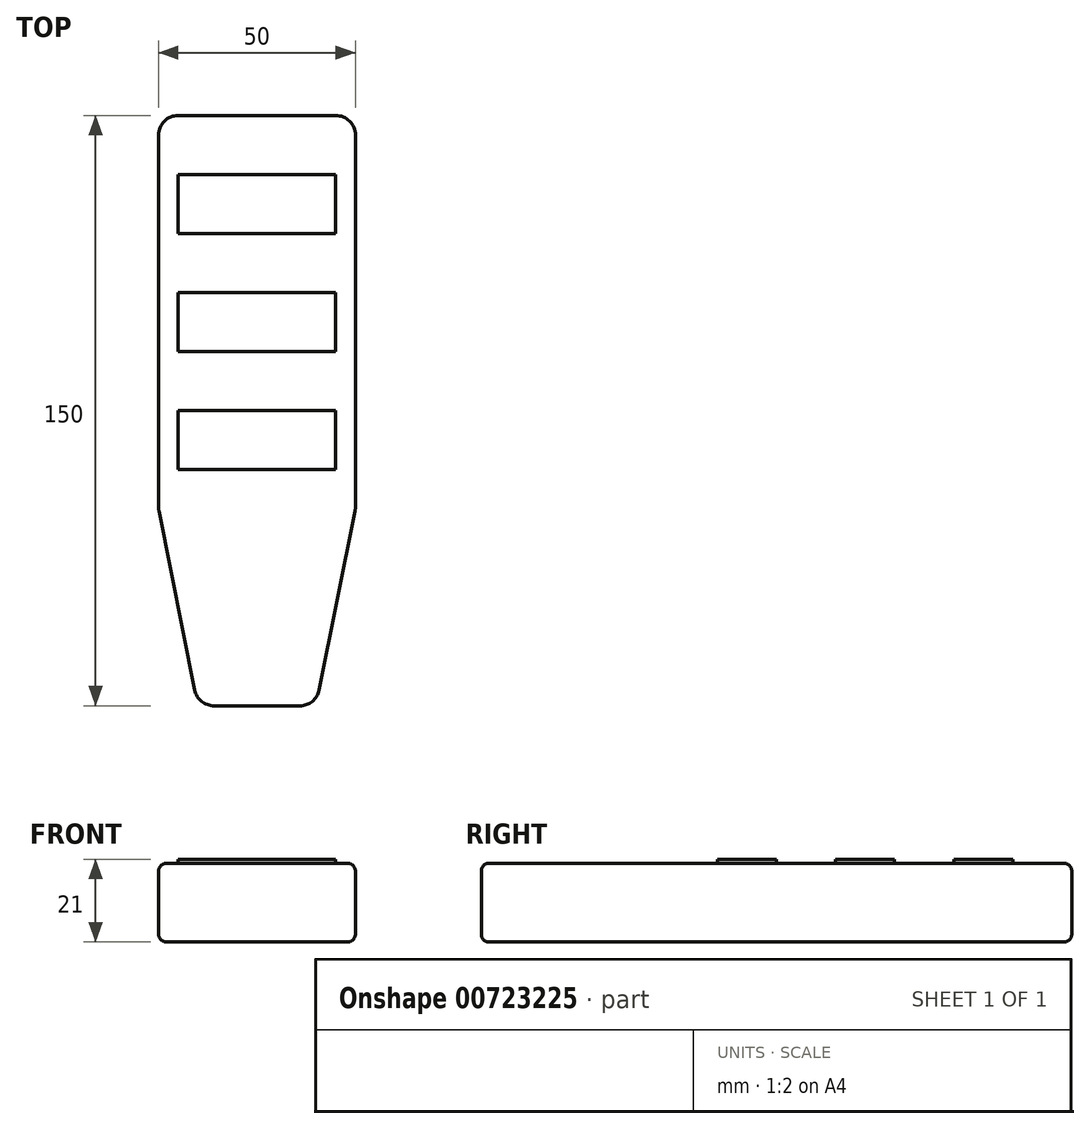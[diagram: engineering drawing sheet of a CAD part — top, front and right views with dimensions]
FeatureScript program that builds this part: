
annotation { "Feature Type Name" : "Feature", "Feature Type Description" : "" }
export const myFeature = defineFeature(function(context is Context, id is Id, definition is map)
    precondition{}
    {
        {
            var Q0;
            Q0=qCreatedBy(makeId("Top.planeOp"),FACE);
            var sketch = newSketch(context, id + "F0", { "sketchPlane" : qUnion([Q0])});
            skLineSegment(sketch, "E0.bottom", {"start": v(-20, 75) * mm, "end": v(20, 75) * mm});
            skLineSegment(sketch, "E0.top", {"start": v(-10.9, -75) * mm, "end": v(10.9, -75) * mm});
            skLineSegment(sketch, "E0.left", {"start": v(-25, 70) * mm, "end": v(-25, -24.5) * mm});
            skLineSegment(sketch, "E0.right", {"start": v(25, 70) * mm, "end": v(25, -24.5) * mm});
            skLineSegment(sketch, "E1", {"start": v(-24.9, -25.49) * mm, "end": v(-15.8, -70.98) * mm});
            skLineSegment(sketch, "E2", {"start": v(24.9, -25.49) * mm, "end": v(15.8, -70.98) * mm});
            skPoint(sketch, "E3.visualSharp", {"position": v(-25, 75) * mm});
            skArc(sketch, "E3.filletArc", {"start": v(-20, 75) * mm, "mid": v(-23.54, 73.54) * mm, "end": v(-25, 70) * mm});
            skPoint(sketch, "E4.visualSharp", {"position": v(25, 75) * mm});
            skArc(sketch, "E4.filletArc", {"start": v(25, 70) * mm, "mid": v(23.54, 73.54) * mm, "end": v(20, 75) * mm});
            skPoint(sketch, "E5.orphan", {"position": v(-25, -75) * mm});
            skPoint(sketch, "E6.orphan", {"position": v(25, -75) * mm});
            skPoint(sketch, "E7.visualSharp", {"position": v(-25, -25) * mm});
            skArc(sketch, "E7.filletArc", {"start": v(-25, -24.5) * mm, "mid": v(-24.98, -25) * mm, "end": v(-24.9, -25.49) * mm});
            skPoint(sketch, "E8.visualSharp", {"position": v(-15, -75) * mm});
            skArc(sketch, "E8.filletArc", {"start": v(-15.8, -70.98) * mm, "mid": v(-14.07, -73.87) * mm, "end": v(-10.9, -75) * mm});
            skPoint(sketch, "E9.visualSharp", {"position": v(15, -75) * mm});
            skArc(sketch, "E9.filletArc", {"start": v(10.9, -75) * mm, "mid": v(14.07, -73.87) * mm, "end": v(15.8, -70.98) * mm});
            skPoint(sketch, "E10.visualSharp", {"position": v(25, -25) * mm});
            skArc(sketch, "E10.filletArc", {"start": v(24.9, -25.49) * mm, "mid": v(24.98, -25) * mm, "end": v(25, -24.5) * mm});
            skSolve(sketch);
        }
        {
            var Q0;
            Q0 = qSketchRegion(id + "F0", true);
            extrude(context, id + "F1", {"entities" : qUnion([Q0]), "depth" : 20 * mm, "offsetDistance" : 25 * mm});
        }
        {
            var Q0;
            Q0=makeQuery(id+"F1.opExtrude","CAP_EDGE",EDGE,{"disambiguationData":[OSD([sQuery(id+"F0.wireOp",EDGE,"E0.left")])],"isStart":false});
            var Q1;
            Q1=makeQuery(id+"F1.opExtrude","CAP_EDGE",EDGE,{"disambiguationData":[OSD([sQuery(id+"F0.wireOp",EDGE,"E1")])],"isStart":true});
            fillet(context, id + "F2", {"entities" : qUnion([Q0, Q1]), "radius" : 2 * mm, "tangentPropagation" : true, "allowEdgeOverflow" : false});
        }
        {
            var Q0;
            Q0=makeQuery(id+"F1.opExtrude","CAP_FACE",FACE,{"disambiguationData":[OSD([sQuery(id+"F0.wireOp",EDGE,"E0.bottom"),sQuery(id+"F0.wireOp",EDGE,"E0.top"),sQuery(id+"F0.wireOp",EDGE,"E0.left"),sQuery(id+"F0.wireOp",EDGE,"E0.right"),sQuery(id+"F0.wireOp",EDGE,"E1"),sQuery(id+"F0.wireOp",EDGE,"E2"),sQuery(id+"F0.wireOp",EDGE,"E3.filletArc"),sQuery(id+"F0.wireOp",EDGE,"E4.filletArc"),sQuery(id+"F0.wireOp",EDGE,"E7.filletArc"),sQuery(id+"F0.wireOp",EDGE,"E8.filletArc"),sQuery(id+"F0.wireOp",EDGE,"E9.filletArc"),sQuery(id+"F0.wireOp",EDGE,"E10.filletArc")])],"isStart":false});
            var sketch = newSketch(context, id + "F3", { "sketchPlane" : qUnion([Q0])});
            skLineSegment(sketch, "E11.bottom", {"start": v(-20, 60) * mm, "end": v(20, 60) * mm});
            skLineSegment(sketch, "E11.top", {"start": v(-20, 45) * mm, "end": v(20, 45) * mm});
            skLineSegment(sketch, "E11.left", {"start": v(-20, 60) * mm, "end": v(-20, 45) * mm});
            skLineSegment(sketch, "E11.right", {"start": v(20, 60) * mm, "end": v(20, 45) * mm});
            skLineSegment(sketch, "E12.0.1.0", {"start": v(-20, 15) * mm, "end": v(20, 15) * mm});
            skLineSegment(sketch, "E12.0.1.1", {"start": v(-20, 30) * mm, "end": v(-20, 15) * mm});
            skLineSegment(sketch, "E12.0.1.2", {"start": v(-20, 30) * mm, "end": v(20, 30) * mm});
            skLineSegment(sketch, "E12.0.1.3", {"start": v(20, 30) * mm, "end": v(20, 15) * mm});
            skLineSegment(sketch, "E12.0.2.0", {"start": v(-20, -15) * mm, "end": v(20, -15) * mm});
            skLineSegment(sketch, "E12.0.2.1", {"start": v(-20, 0) * mm, "end": v(-20, -15) * mm});
            skLineSegment(sketch, "E12.0.2.2", {"start": v(-20, 0) * mm, "end": v(20, 0) * mm});
            skLineSegment(sketch, "E12.0.2.3", {"start": v(20, 0) * mm, "end": v(20, -15) * mm});
            skLineSegment(sketch, "E12.direction1", {"start": v(-20, 45) * mm, "end": v(5, 45) * mm, "construction": true});
            skLineSegment(sketch, "E12.direction2", {"start": v(-20, 45) * mm, "end": v(-20, 15) * mm, "construction": true});
            skSolve(sketch);
        }
        {
            var Q0;
            Q0=makeQuery(id+"F3.imprint","IMPRINT",FACE,{"disambiguationData":[TD([[makeQuery(id+"F3.imprint","IMPRINT",EDGE,{"derivedFrom":sQuery(id+"F3.wireOp",EDGE,"E11.bottom")}),-1.0]])]});
            var Q1;
            Q1=makeQuery(id+"F3.imprint","IMPRINT",FACE,{"disambiguationData":[TD([[makeQuery(id+"F3.imprint","IMPRINT",EDGE,{"derivedFrom":sQuery(id+"F3.wireOp",EDGE,"E12.0.1.0")}),1.0]])]});
            var Q2;
            Q2=makeQuery(id+"F3.imprint","IMPRINT",FACE,{"disambiguationData":[TD([[makeQuery(id+"F3.imprint","IMPRINT",EDGE,{"derivedFrom":sQuery(id+"F3.wireOp",EDGE,"E12.0.2.0")}),1.0]])]});
            extrude(context, id + "F4", {"entities" : qUnion([Q0, Q1, Q2]), "operationType" : NewBodyOperationType.ADD, "depth" : 1 * mm, "offsetDistance" : 25 * mm});
        }
    });
